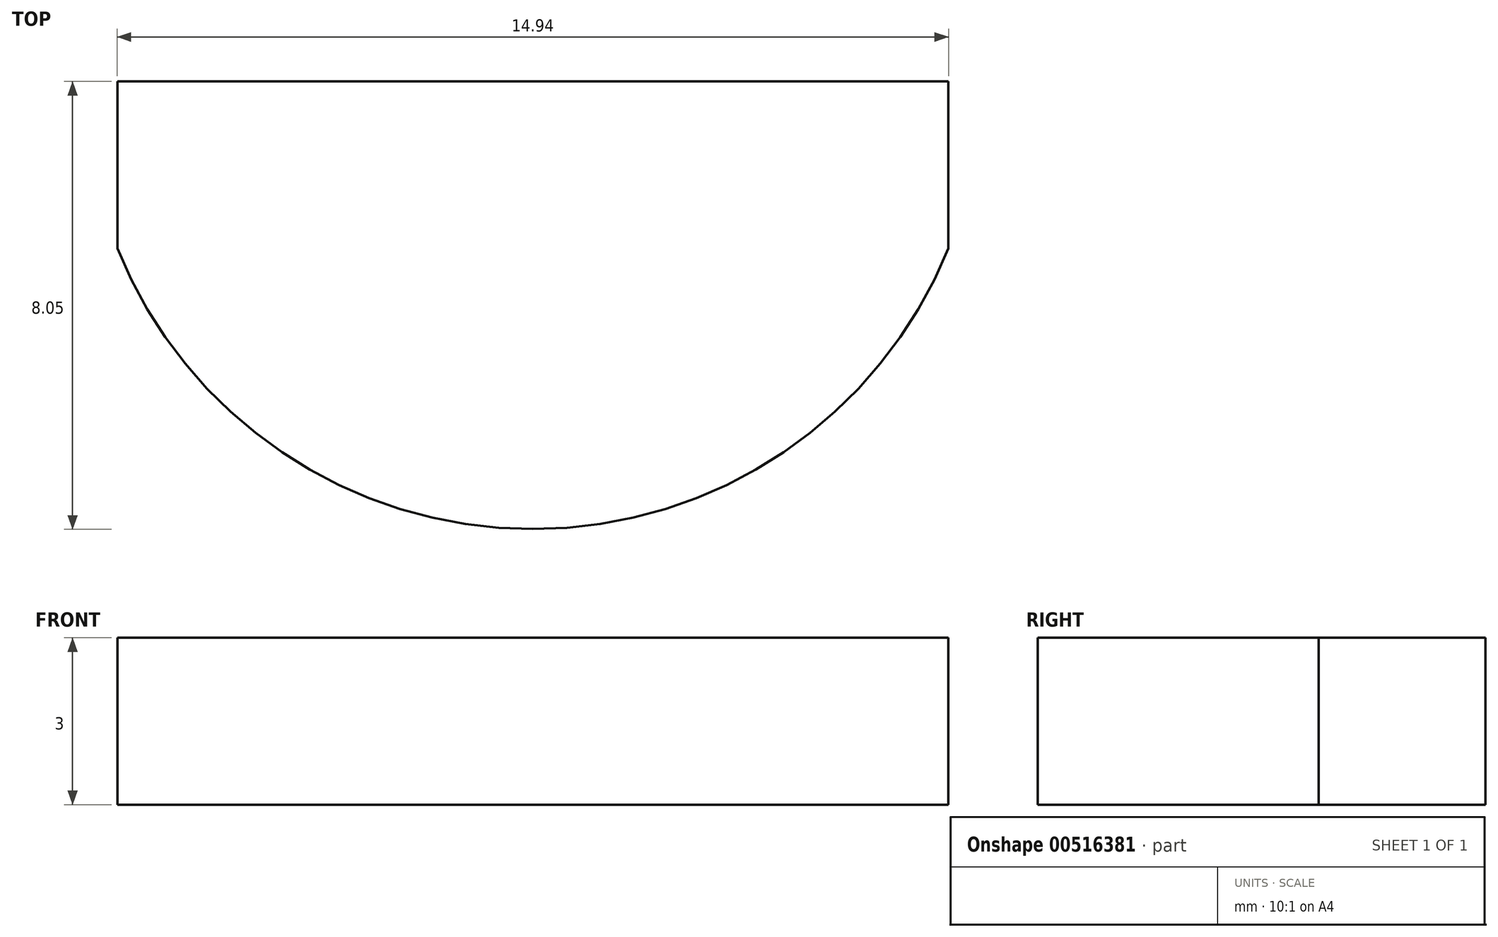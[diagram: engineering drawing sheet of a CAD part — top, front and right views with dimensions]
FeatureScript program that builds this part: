
annotation { "Feature Type Name" : "Feature", "Feature Type Description" : "" }
export const myFeature = defineFeature(function(context is Context, id is Id, definition is map)
    precondition{}
    {
        {
            var Q0;
            Q0=qCreatedBy(makeId("Top.planeOp"),FACE);
            var sketch = newSketch(context, id + "F0", { "sketchPlane" : qUnion([Q0])});
            skArc(sketch, "E0", {"start": v(-7.47, -3) * mm, "mid": v(0, -8.05) * mm, "end": v(7.47, -3) * mm});
            skLineSegment(sketch, "E1", {"start": v(0, -3) * mm, "end": v(7.47, -3) * mm});
            skLineSegment(sketch, "E2", {"start": v(7.47, -3) * mm, "end": v(-7.47, -3) * mm});
            skLineSegment(sketch, "E3", {"start": v(-7.47, -3) * mm, "end": v(-7.47, 0) * mm});
            skLineSegment(sketch, "E4", {"start": v(-7.47, 0) * mm, "end": v(0, 0) * mm});
            skLineSegment(sketch, "E5", {"start": v(7.47, -3) * mm, "end": v(7.47, 0) * mm});
            skLineSegment(sketch, "E6", {"start": v(7.47, 0) * mm, "end": v(0, 0) * mm});
            skSolve(sketch);
        }
        {
            var Q0;
            {var subQ0=sQuery(id+"F0.wireOp",EDGE,"E0");Q0=makeQuery(id+"F0.imprint","IMPRINT",FACE,{"disambiguationData":[TD([[makeQuery(id+"F0.imprint","IMPRINT",EDGE,{"derivedFrom":subQ0}),1.0]])]});}
            var Q1;
            {var subQ0=sQuery(id+"F0.wireOp",EDGE,"E3");Q1=makeQuery(id+"F0.imprint","IMPRINT",FACE,{"disambiguationData":[TD([[makeQuery(id+"F0.imprint","IMPRINT",EDGE,{"derivedFrom":subQ0}),-1.0]])]});}
            extrude(context, id + "F1", {"entities" : qUnion([Q0, Q1]), "depth" : 3 * mm, "offsetDistance" : 25 * mm});
        }
    });
